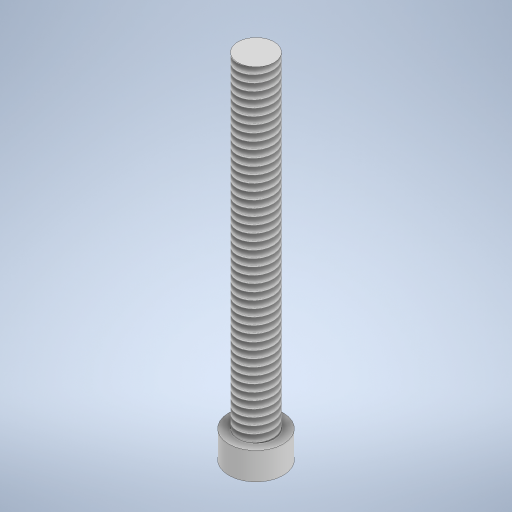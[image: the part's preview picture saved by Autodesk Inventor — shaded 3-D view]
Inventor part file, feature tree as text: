
AUTODESK INVENTOR PART (.ipt)
format: ipt  version: 2024.2 (Build 282272000, 272)  size: 281,088 bytes
history: native  units: mm
features: extrude x2, sketch x2, thread x1
ambient origin geometry x8: Origin, YZ Plane, XZ Plane, XY Plane, X Axis, Y Axis, Z Axis, Center Point
bodies: Solid1 (feature_tree)
feature tree (5):
  extrude  "Extrusion1"  Depth=1.5mm TaperAngle=0.0deg
  extrude  "Extrusion2"  Depth=18.0mm TaperAngle=0.0deg
  thread  "Thread1"  [1 undecoded]
  sketch  "Sketch1"  dims[d0=3.0mm d1=1.5mm d2=0.0mm]
  sketch  "Sketch2"  dims[d3=2.0mm d4=18.0mm d5=0.0mm d6=18.0mm d7=0.0mm]
note: 1 required parameter value undecoded (feature->parameter linkage not recoverable at this tier; creation-order binding heuristic only, values carry confidence <= 0.55)
